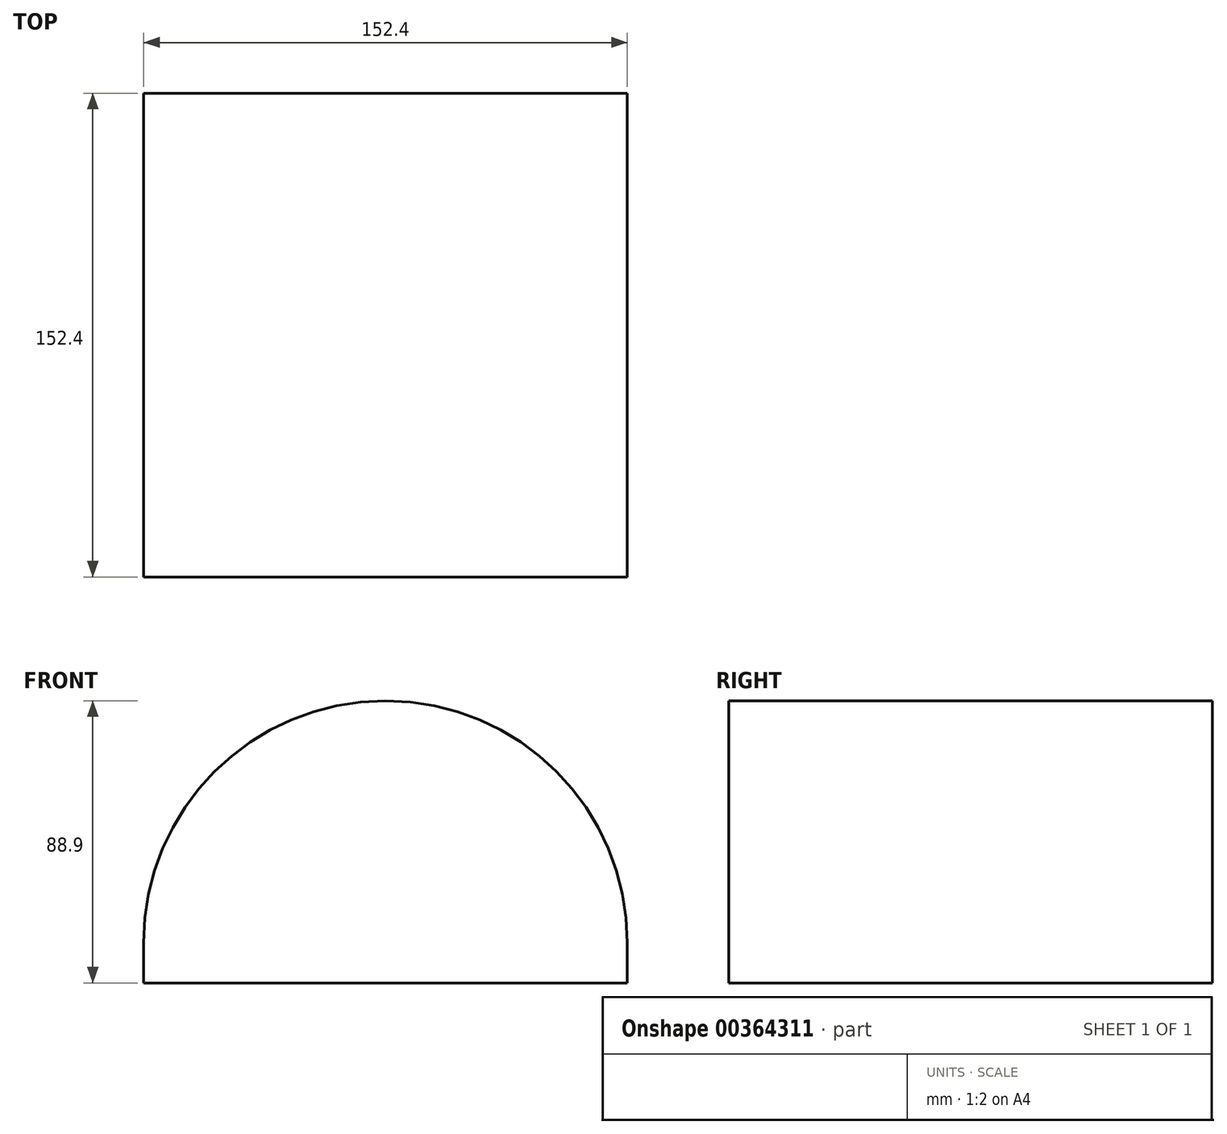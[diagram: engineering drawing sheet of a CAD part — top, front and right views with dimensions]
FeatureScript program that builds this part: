
annotation { "Feature Type Name" : "Feature", "Feature Type Description" : "" }
export const myFeature = defineFeature(function(context is Context, id is Id, definition is map)
    precondition{}
    {
        {
            var Q0;
            Q0=qCreatedBy(makeId("Front.planeOp"),FACE);
            var sketch = newSketch(context, id + "F0", { "sketchPlane" : qUnion([Q0])});
            skLineSegment(sketch, "E0", {"start": v(76.2, 0) * mm, "end": v(-76.2, 0) * mm});
            skPoint(sketch, "E1.end.orphan", {"position": v(76.2, 0) * mm});
            skLineSegment(sketch, "E2", {"start": v(-76.2, 0) * mm, "end": v(-76.2, 12.7) * mm});
            skLineSegment(sketch, "E3", {"start": v(-76.2, 12.7) * mm, "end": v(-76.2, 12.7) * mm});
            skLineSegment(sketch, "E4", {"start": v(76.2, 0) * mm, "end": v(76.2, 12.7) * mm});
            skLineSegment(sketch, "E5", {"start": v(76.2, 12.7) * mm, "end": v(76.2, 12.7) * mm});
            skArc(sketch, "E6", {"start": v(76.2, 12.7) * mm, "mid": v(0, 88.9) * mm, "end": v(-76.2, 12.7) * mm});
            skSolve(sketch);
        }
        {
            var Q0;
            Q0=makeQuery(id+"F0.imprint","IMPRINT",FACE,{"disambiguationData":[TD([[makeQuery(id+"F0.imprint","IMPRINT",EDGE,{"derivedFrom":sQuery(id+"F0.wireOp",EDGE,"E0")}),-1.0]])]});
            extrude(context, id + "F1", {"entities" : qUnion([Q0]), "endBound" : BoundingType.SYMMETRIC, "depth" : 152.4 * mm});
        }
    });
